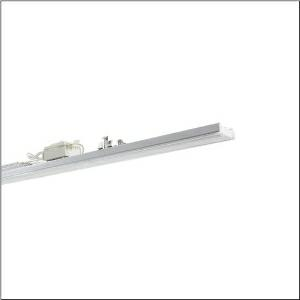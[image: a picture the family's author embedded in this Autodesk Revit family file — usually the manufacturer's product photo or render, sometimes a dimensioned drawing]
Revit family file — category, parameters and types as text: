
# Revit family: licross_r__21_recessed_mo_52te117n485g_1cb6
name_source: partatom
category: Lighting Fixtures
units: mm (PartAtom-declared; Revit-internal decimal feet)

## family parameters
Cut with Voids When Loaded = No
Host = Face
Light Source = No
Part Type = Normal
Room Calculation Point = No
Round Connector Dimension = Use Diameter
Shared = No

## types (1)
- Licross® 21 Recessed MO (1 x LED, 8680 lm, 47.9 W, 4000K)
    Apparent Load = 48 VA
    CIE Flux Codes = 89 96 99 100 100
    Color Rendering = 80
    Color Temperature = 4000K
    Default Elevation = 1800 mm
    Description = Licross® 21 Recessed MO, luminaire insert, of sheet steel, galvanised, coil coated, white, length: 1.500mm, width: 66mm, height: 67mm, LED rated luminous flux: 8.680lm, light colour: 840, control gear: ON/OFF, with plug, 3-pole, with phase selection, mains connection: 220..240V, AC, 50/60Hz, rated input power: 48W, internal wiring halogen-free, primary light control with lens, of plastic, primary optical cover: cover, of PMMA, light emission: direct distribution, primary light characteristic: symmetric, protection rating (complete): IP54, insulation class (complete): insulation class I (protective earthing), certification: CE, ENEC, VDE, UKCA, protection symbol: D if used in an environment with non-conductive dust loads with corresponding accessories, impact resistance: IK06, permissible ambient temperature for indoor applications: -35..+40°C, corresponds to IFS (International Featured Standards) requirements for safety and quality in the food industry, reducing of maximum allowable ambient temperature of 5°C with ceiling mounting, LABS conformity tested according to VDMA 24364:2018-05, packaging unit: 1 piece
    Height = 58 mm
    Lamp = 1 x LED
    Lamp Light Flux = 8680 lm
    Lamp Power = 47.9 W
    Lamp count = 1
    Length = 1500 mm
    Luminous efficacy = 181 lm/W
    Manufacturer = Siteco
    ModVariant = No
    Model = 52TE117N485G
    Mounting Place = Ceiling
    Mounting Type = Pendant
    Number of Poles = 1
    OnlyDefault = Yes
    Power Factor = 1
    Product Name = Licross® 21 Recessed MO
    Product group = luminaire insert | ceiling pendant
    ProductGroupID = 902
    Protection Class = Protection class I
    Protection Degree = IP 54
    RLX_Detail_Level = 1
    RLX_Emergency_Light_Flux = 0 lm
    RLX_Emergency_Type = 0
    RLX_Emergency_Type_DB = No
    RlxData = <blob elided: 20877 chars, md5=aa02ffc4>
    Socket = socket
    Standby Power = 0 W
    System Light Flux = 8680 lm
    System Power = 48 W
    Type Comments = Product without accessories
    Type Image = l_1296930.jpg
    URL = http://relux.com
    VarID = ---
    Voltage = 0 V
    Weight = 0.00 kg
    Width = 66 mm

## geometry (parser evidence)
native form markers: Blend x4, Sweep x9
no freeform markers — native parametric forms only
